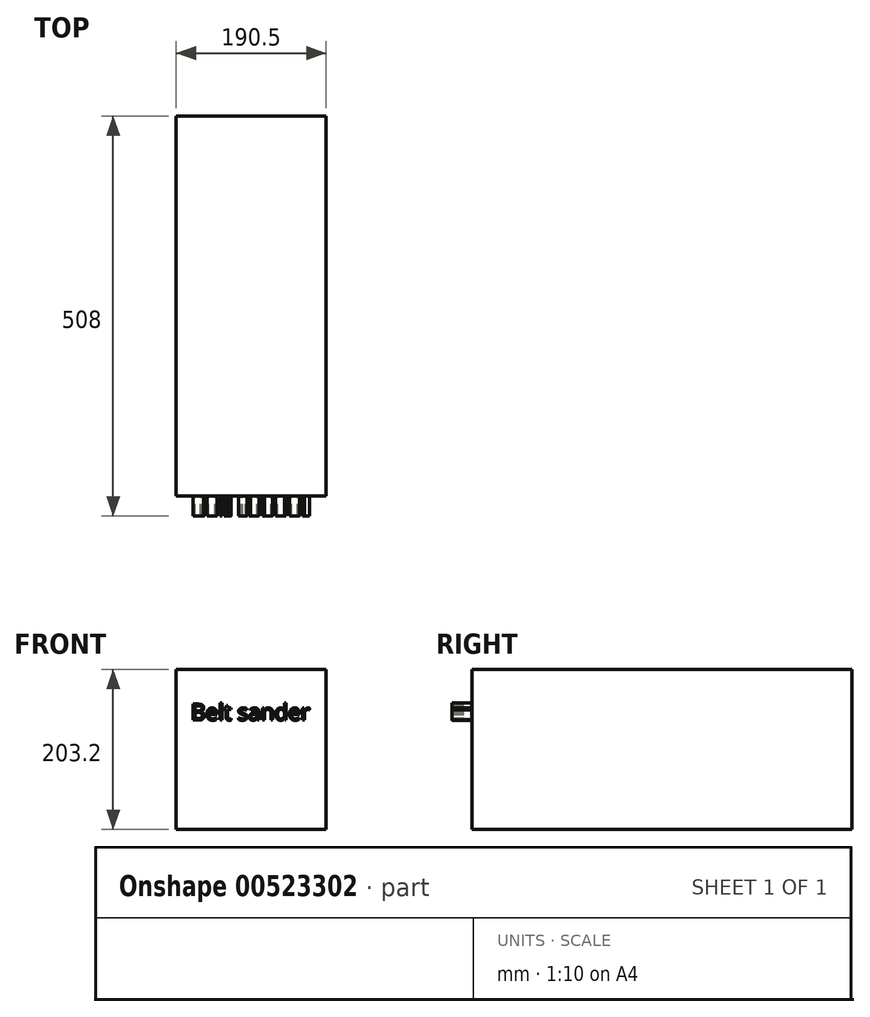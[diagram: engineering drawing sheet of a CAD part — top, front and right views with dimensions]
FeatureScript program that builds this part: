
annotation { "Feature Type Name" : "Feature", "Feature Type Description" : "" }
export const myFeature = defineFeature(function(context is Context, id is Id, definition is map)
    precondition{}
    {
        {
            var Q0;
            Q0=qCreatedBy(makeId("Front.planeOp"),FACE);
            var sketch = newSketch(context, id + "F0", { "sketchPlane" : qUnion([Q0])});
            skLineSegment(sketch, "E0.bottom", {"start": v(95.25, 101.6) * mm, "end": v(-95.25, 101.6) * mm});
            skLineSegment(sketch, "E0.top", {"start": v(95.25, -101.6) * mm, "end": v(-95.25, -101.6) * mm});
            skLineSegment(sketch, "E0.left", {"start": v(95.25, 101.6) * mm, "end": v(95.25, -101.6) * mm});
            skLineSegment(sketch, "E0.right", {"start": v(-95.25, 101.6) * mm, "end": v(-95.25, -101.6) * mm});
            skPoint(sketch, "E0.middle", {"position": v(0, 0) * mm});
            skSolve(sketch);
        }
        {
            var Q0;
            Q0=makeQuery(id+"F0.imprint","IMPRINT",FACE,{"disambiguationData":[TD([[makeQuery(id+"F0.imprint","IMPRINT",EDGE,{"derivedFrom":sQuery(id+"F0.wireOp",EDGE,"E0.bottom")}),1.0]])]});
            extrude(context, id + "F1", {"entities" : qUnion([Q0]), "depth" : 482.6 * mm, "offsetDistance" : 25.4 * mm});
        }
        {
            var Q0;
            Q0=makeQuery(id+"F1.opExtrude","CAP_FACE",FACE,{"disambiguationData":[OSD([sQuery(id+"F0.wireOp",EDGE,"E0.bottom"),sQuery(id+"F0.wireOp",EDGE,"E0.top"),sQuery(id+"F0.wireOp",EDGE,"E0.left"),sQuery(id+"F0.wireOp",EDGE,"E0.right")])],"isStart":false});
            var sketch = newSketch(context, id + "F2", { "sketchPlane" : qUnion([Q0])});
            skText(sketch, "E1", { "text": "Belt sander", "fontName": "OpenSans-Regular.ttf"});
            const initialGuessF2  = {"E1": [-0.07638, 0.03726, 1, 0, 0.0205]};
            skSetInitialGuess(sketch, initialGuessF2);
            skSolve(sketch);
        }
        {
            var Q0;
            Q0 = qSketchRegion(id + "F2", true);
            extrude(context, id + "F3", {"entities" : qUnion([Q0]), "operationType" : NewBodyOperationType.ADD, "depth" : 25.4 * mm, "offsetDistance" : 25.4 * mm});
        }
    });
